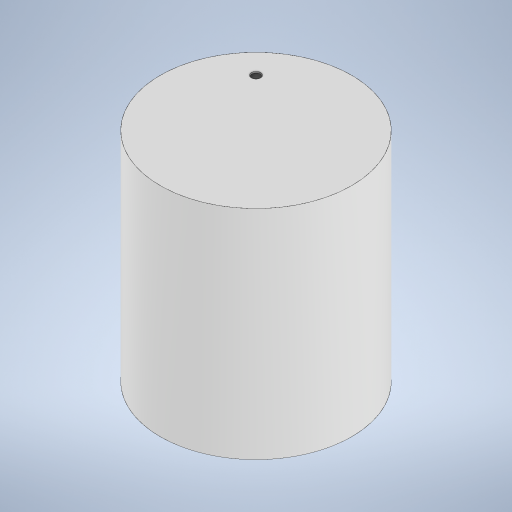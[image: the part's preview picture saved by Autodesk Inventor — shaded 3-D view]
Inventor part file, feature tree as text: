
AUTODESK INVENTOR PART (.ipt)
format: ipt  version: 2024 (Build 280153000, 153)  size: 244,736 bytes
history: native  units: mm
features: extrude x4, sketch x4
ambient origin geometry x8: Origin, YZ Plane, XZ Plane, XY Plane, X Axis, Y Axis, Z Axis, Center Point
bodies: Solid1 (feature_tree)
feature tree (8):
  extrude  "Extrusion1"  Depth=278.0mm
  extrude  "Extrusion2"  Depth=2.0mm TaperAngle=0.0deg
  extrude  "Extrusion3"  Depth=2.0mm
  extrude  "Extrusion9"  Depth=10.0mm
  sketch  "Sketch1"  dims[d0=285.0mm d1=278.0mm]
  sketch  "Sketch2"  dims[d2=320.0mm d3=0.0mm d4=2.0mm d5=0.0mm]
  sketch  "Sketch3"  dims[d6=2.0mm d7=0.0mm d8=14.0mm]
  sketch  "Sketch4"  dims[d23=10.0mm d24=0.0mm d11=0.5mm d12=0.872665mm d13=0.5mm d14=0.872665mm]
